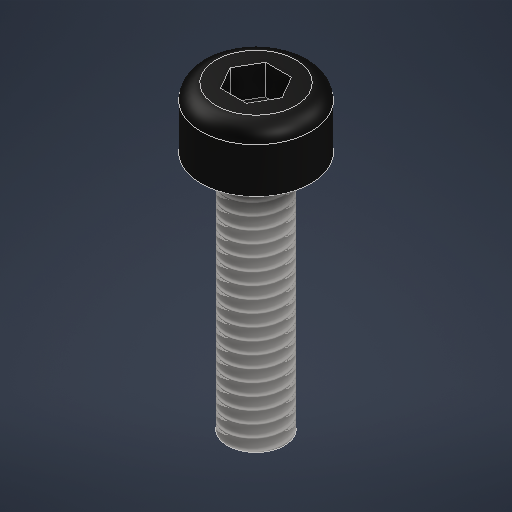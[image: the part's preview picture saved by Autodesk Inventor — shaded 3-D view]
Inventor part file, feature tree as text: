
AUTODESK INVENTOR PART (.ipt)
format: ipt  version: 2025.1 (Build 291241000, 241)  size: 268,800 bytes
history: native  units: mm
features: extrude x3, sketch x1, fillet x1, thread x1
ambient origin geometry x8: Origin, YZ Plane, XZ Plane, XY Plane, X Axis, Y Axis, Z Axis, Center Point
bodies: Solid1 (feature_tree)
feature tree (6):
  sketch  "Sketch1"  dims[d0=1.9mm d1=3.65mm d2=2.0mm d3=0.0mm d4=8.0mm d5=0.0mm d8=1.5mm d9=1.0mm d10=0.0mm d11=0.5mm d12=16.0mm d13=0.0mm]
  extrude  "Extrusion1"  Depth=0.5mm
  extrude  "Extrusion2"  Depth=2.0mm TaperAngle=0.0deg
  extrude  "Extrusion3"  Depth=8.0mm
  fillet  "Fillet1"  [1 undecoded]
  thread  "Thread2"  [1 undecoded]
note: 2 required parameter values undecoded (feature->parameter linkage not recoverable at this tier; creation-order binding heuristic only, values carry confidence <= 0.55)
